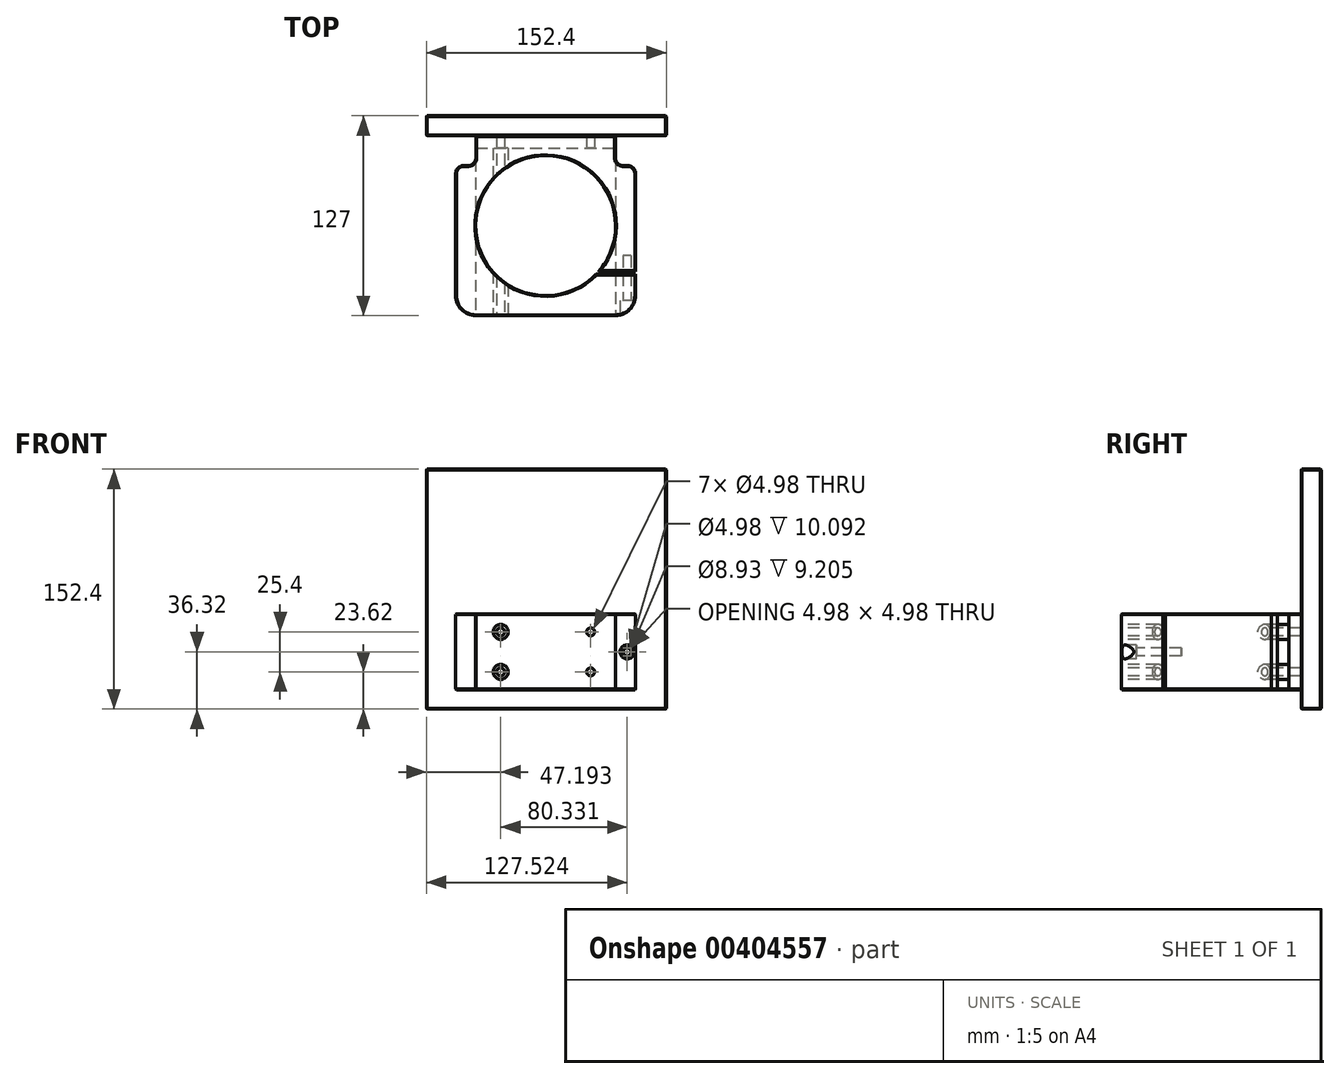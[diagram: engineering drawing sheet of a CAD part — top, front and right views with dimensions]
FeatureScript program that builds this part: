
annotation { "Feature Type Name" : "Feature", "Feature Type Description" : "" }
export const myFeature = defineFeature(function(context is Context, id is Id, definition is map)
    precondition{}
    {
        {
            var Q0;
            Q0=qCreatedBy(makeId("Front.planeOp"),FACE);
            var sketch = newSketch(context, id + "F0", { "sketchPlane" : qUnion([Q0])});
            skLineSegment(sketch, "E0.bottom", {"start": v(57.15, 57.15) * mm, "end": v(-57.15, 57.15) * mm});
            skLineSegment(sketch, "E0.top", {"start": v(57.15, -57.15) * mm, "end": v(-57.15, -57.15) * mm});
            skLineSegment(sketch, "E0.left", {"start": v(57.15, 57.15) * mm, "end": v(57.15, -57.15) * mm});
            skLineSegment(sketch, "E0.right", {"start": v(-57.15, 57.15) * mm, "end": v(-57.15, -57.15) * mm});
            skPoint(sketch, "E0.middle", {"position": v(0, 0) * mm});
            skLineSegment(sketch, "E1", {"start": v(-57.15, 38.1) * mm, "end": v(-44.28, 38.1) * mm});
            skLineSegment(sketch, "E2", {"start": v(-44.28, 57.15) * mm, "end": v(-44.28, 38.1) * mm});
            skLineSegment(sketch, "E3.MirrorCS", {"start": v(44.28, 57.15) * mm, "end": v(44.28, 38.1) * mm});
            skCircle(sketch, "E4", {"center": v(0, 0) * mm, "radius": 44.45 * mm});
            skLineSegment(sketch, "E5.trimOffspring", {"start": v(44.28, 38.1) * mm, "end": v(57.15, 38.1) * mm});
            skSolve(sketch);
        }
        {
            var Q0;
            {var subQ1=sQuery(id+"F0.wireOp",EDGE,"E0.top");Q0=makeQuery(id+"F0.imprint","IMPRINT",FACE,{"disambiguationData":[TD([[makeQuery(id+"F0.imprint","IMPRINT",EDGE,{"derivedFrom":subQ1}),-1.0]])]});}
            extrude(context, id + "F1", {"entities" : qUnion([Q0]), "depth" : 48.26 * mm});
        }
        {
            var Q0;
            Q0=makeQuery(id+"F1.opExtrude","SWEPT_EDGE",EDGE,{"disambiguationData":[OSD([sQuery(id+"F0.wireOp",EDGE,"E3.MirrorCS"),sQuery(id+"F0.wireOp",EDGE,"E5.trimOffspring")])]});
            var Q1;
            Q1=makeQuery(id+"F1.opExtrude","SWEPT_EDGE",EDGE,{"disambiguationData":[OSD([sQuery(id+"F0.wireOp",EDGE,"E0.left"),sQuery(id+"F0.wireOp",EDGE,"E5.trimOffspring")])]});
            var Q2;
            Q2=makeQuery(id+"F1.opExtrude","SWEPT_EDGE",EDGE,{"disambiguationData":[OSD([sQuery(id+"F0.wireOp",EDGE,"E1"),sQuery(id+"F0.wireOp",EDGE,"E2")])]});
            var Q3;
            Q3=makeQuery(id+"F1.opExtrude","SWEPT_EDGE",EDGE,{"disambiguationData":[OSD([sQuery(id+"F0.wireOp",EDGE,"E0.right"),sQuery(id+"F0.wireOp",EDGE,"E1")])]});
            fillet(context, id + "F2", {"entities" : qUnion([Q0, Q1, Q2, Q3]), "radius" : 5.08 * mm, "tangentPropagation" : true, "allowEdgeOverflow" : false});
        }
        {
            var Q0;
            Q0=makeQuery(id+"F1.opExtrude","SWEPT_EDGE",EDGE,{"disambiguationData":[OSD([sQuery(id+"F0.wireOp",EDGE,"E0.top"),sQuery(id+"F0.wireOp",EDGE,"E0.left")])]});
            var Q1;
            Q1=makeQuery(id+"F1.opExtrude","SWEPT_EDGE",EDGE,{"disambiguationData":[OSD([sQuery(id+"F0.wireOp",EDGE,"E0.top"),sQuery(id+"F0.wireOp",EDGE,"E0.right")])]});
            fillet(context, id + "F3", {"entities" : qUnion([Q0, Q1]), "radius" : 12.7 * mm, "tangentPropagation" : true, "allowEdgeOverflow" : false});
        }
        {
            var Q0;
            Q0=makeQuery(id+"F1.opExtrude","CAP_FACE",FACE,{"disambiguationData":[OSD([sQuery(id+"F0.wireOp",EDGE,"E0.bottom"),sQuery(id+"F0.wireOp",EDGE,"E0.top"),sQuery(id+"F0.wireOp",EDGE,"E0.left"),sQuery(id+"F0.wireOp",EDGE,"E0.right"),sQuery(id+"F0.wireOp",EDGE,"E1"),sQuery(id+"F0.wireOp",EDGE,"E2"),sQuery(id+"F0.wireOp",EDGE,"E3.MirrorCS"),sQuery(id+"F0.wireOp",EDGE,"E4"),sQuery(id+"F0.wireOp",EDGE,"E5.trimOffspring")])],"isStart":true});
            var sketch = newSketch(context, id + "F4", { "sketchPlane" : qUnion([Q0])});
            skLineSegment(sketch, "E6.bottom", {"start": v(70.96, -29.14) * mm, "end": v(-5.24, -29.14) * mm});
            skLineSegment(sketch, "E6.top", {"start": v(70.96, -30.73) * mm, "end": v(-5.24, -30.73) * mm});
            skLineSegment(sketch, "E6.left", {"start": v(70.96, -29.14) * mm, "end": v(70.96, -30.73) * mm});
            skLineSegment(sketch, "E6.right", {"start": v(-5.24, -29.14) * mm, "end": v(-5.24, -30.73) * mm});
            skPoint(sketch, "E6.middle", {"position": v(32.86, -29.94) * mm});
            skSolve(sketch);
        }
        {
            var Q0;
            {var subQ0=sQuery(id+"F4.wireOp",EDGE,"E6.bottom");var subQ1=makeQuery(id+"F1.opExtrude","CAP_EDGE",EDGE,{"disambiguationData":[OSD([sQuery(id+"F0.wireOp",EDGE,"E0.right")])],"isStart":true});var subQ2=makeQuery(id+"F4.imprint","INTERSECT",VERTEX,{"derivedFrom":[subQ1,subQ0]});Q0=makeQuery(id+"F4.imprint","IMPRINT",FACE,{"disambiguationData":[TD([[makeQuery(id+"F4.imprint","IMPRINT",EDGE,{"disambiguationData":[TD([[subQ2,-1.0]])],"derivedFrom":subQ0}),1.0]])]});}
            extrude(context, id + "F5", {"entities" : qUnion([Q0]), "operationType" : NewBodyOperationType.REMOVE, "oppositeDirection" : true, "depth" : 50.8 * mm});
        }
        {
            var Q0;
            Q0=makeQuery(id+"F1.opExtrude","CAP_FACE",FACE,{"disambiguationData":[OSD([sQuery(id+"F0.wireOp",EDGE,"E0.bottom"),sQuery(id+"F0.wireOp",EDGE,"E0.top"),sQuery(id+"F0.wireOp",EDGE,"E0.left"),sQuery(id+"F0.wireOp",EDGE,"E0.right"),sQuery(id+"F0.wireOp",EDGE,"E1"),sQuery(id+"F0.wireOp",EDGE,"E2"),sQuery(id+"F0.wireOp",EDGE,"E3.MirrorCS"),sQuery(id+"F0.wireOp",EDGE,"E4"),sQuery(id+"F0.wireOp",EDGE,"E5.trimOffspring")])],"isStart":true});
            var Q1;
            Q1=makeQuery(id+"F1.opExtrude","CAP_FACE",FACE,{"disambiguationData":[OSD([sQuery(id+"F0.wireOp",EDGE,"E0.bottom"),sQuery(id+"F0.wireOp",EDGE,"E0.top"),sQuery(id+"F0.wireOp",EDGE,"E0.left"),sQuery(id+"F0.wireOp",EDGE,"E0.right"),sQuery(id+"F0.wireOp",EDGE,"E1"),sQuery(id+"F0.wireOp",EDGE,"E2"),sQuery(id+"F0.wireOp",EDGE,"E3.MirrorCS"),sQuery(id+"F0.wireOp",EDGE,"E4"),sQuery(id+"F0.wireOp",EDGE,"E5.trimOffspring")])],"isStart":false});
            chamfer(context, id + "F6", {"entities" : qUnion([Q0, Q1]), "width" : 0.5 * mm, "tangentPropagation" : true});
        }
        {
            var Q0;
            Q0=makeQuery(id+"F1.opExtrude","SWEPT_FACE",FACE,{"disambiguationData":[OSD([sQuery(id+"F0.wireOp",EDGE,"E0.top")])]});
            var sketch = newSketch(context, id + "F7", { "sketchPlane" : qUnion([Q0])});
            skLineSegment(sketch, "E7", {"start": v(-44.45, 11.43) * mm, "end": v(44.45, 11.43) * mm, "construction": true});
            skLineSegment(sketch, "E8.MirrorCS", {"start": v(-44.45, 36.83) * mm, "end": v(44.45, 36.83) * mm, "construction": true});
            skLineSegment(sketch, "E9", {"start": v(0, 36.83) * mm, "end": v(0, 11.43) * mm, "construction": true});
            skLineSegment(sketch, "E10", {"start": v(-28.57, 36.83) * mm, "end": v(-28.57, 11.43) * mm, "construction": true});
            skLineSegment(sketch, "E11.MirrorCS", {"start": v(28.58, 36.83) * mm, "end": v(28.58, 11.43) * mm, "construction": true});
            skCircle(sketch, "E12", {"center": v(-28.57, 36.83) * mm, "radius": 2.49 * mm});
            skCircle(sketch, "E13", {"center": v(-28.57, 11.43) * mm, "radius": 2.49 * mm});
            skCircle(sketch, "E14.MirrorC", {"center": v(28.58, 36.83) * mm, "radius": 2.49 * mm});
            skCircle(sketch, "E15.MirrorC", {"center": v(28.58, 11.43) * mm, "radius": 2.49 * mm});
            skSolve(sketch);
        }
        {
            var Q0;
            Q0 = qSketchRegion(id + "F7", true);
            extrude(context, id + "F8", {"entities" : qUnion([Q0]), "operationType" : NewBodyOperationType.REMOVE, "endBound" : BoundingType.THROUGH_ALL, "oppositeDirection" : true, "depth" : 25.4 * mm});
        }
        {
            var Q0;
            Q0=makeQuery(id+"F1.opExtrude","SWEPT_FACE",FACE,{"disambiguationData":[OSD([sQuery(id+"F0.wireOp",EDGE,"E0.top")])]});
            var sketch = newSketch(context, id + "F9", { "sketchPlane" : qUnion([Q0])});
            skCircle(sketch, "E16", {"center": v(-28.57, 36.83) * mm, "radius": 4.76 * mm});
            skCircle(sketch, "E17", {"center": v(-28.57, 11.43) * mm, "radius": 4.76 * mm});
            skCircle(sketch, "E18.MirrorC", {"center": v(28.57, 36.83) * mm, "radius": 4.76 * mm});
            skCircle(sketch, "E19.MirrorC", {"center": v(28.57, 11.43) * mm, "radius": 4.76 * mm});
            skSolve(sketch);
        }
        {
            var Q0;
            Q0=makeQuery(id+"F9.imprint","IMPRINT",FACE,{"disambiguationData":[TD([[makeQuery(id+"F9.imprint","IMPRINT",EDGE,{"derivedFrom":sQuery(id+"F9.wireOp",EDGE,"E17")}),1.0]])]});
            var Q1;
            Q1=makeQuery(id+"F9.imprint","IMPRINT",FACE,{"disambiguationData":[TD([[makeQuery(id+"F9.imprint","IMPRINT",EDGE,{"derivedFrom":sQuery(id+"F9.wireOp",EDGE,"E16")}),1.0]])]});
            var Q2;
            Q2=makeQuery(id+"F9.imprint","IMPRINT",FACE,{"disambiguationData":[TD([[makeQuery(id+"F9.imprint","IMPRINT",EDGE,{"derivedFrom":sQuery(id+"F9.wireOp",EDGE,"E18.MirrorC")}),-1.0]])]});
            var Q3;
            Q3=makeQuery(id+"F9.imprint","IMPRINT",FACE,{"disambiguationData":[TD([[makeQuery(id+"F9.imprint","IMPRINT",EDGE,{"derivedFrom":sQuery(id+"F9.wireOp",EDGE,"E19.MirrorC")}),-1.0]])]});
            extrude(context, id + "F10", {"entities" : qUnion([Q0, Q1, Q2, Q3]), "operationType" : NewBodyOperationType.REMOVE, "oppositeDirection" : true, "depth" : 106.43 * mm});
        }
        {
            var Q0;
            Q0=makeQuery(id+"F1.opExtrude","SWEPT_FACE",FACE,{"disambiguationData":[OSD([sQuery(id+"F0.wireOp",EDGE,"E0.bottom")])]});
            var sketch = newSketch(context, id + "F11", { "sketchPlane" : qUnion([Q0])});
            skLineSegment(sketch, "E20.bottom", {"start": v(75.77, -47.75) * mm, "end": v(-76.63, -47.75) * mm});
            skLineSegment(sketch, "E20.top", {"start": v(75.77, 104.65) * mm, "end": v(-76.63, 104.65) * mm});
            skLineSegment(sketch, "E20.left", {"start": v(75.77, -47.75) * mm, "end": v(75.77, 104.65) * mm});
            skLineSegment(sketch, "E20.right", {"start": v(-76.63, -47.75) * mm, "end": v(-76.63, 104.65) * mm});
            skSolve(sketch);
        }
        {
            var Q0;
            Q0 = qSketchRegion(id + "F11", true);
            extrude(context, id + "F12", {"entities" : qUnion([Q0]), "depth" : 12.7 * mm});
        }
        {
            var Q0;
            Q0=makeQuery(id+"F12.opExtrude","CAP_FACE",FACE,{"disambiguationData":[OSD([sQuery(id+"F11.wireOp",EDGE,"E20.bottom"),sQuery(id+"F11.wireOp",EDGE,"E20.top"),sQuery(id+"F11.wireOp",EDGE,"E20.left"),sQuery(id+"F11.wireOp",EDGE,"E20.right")])],"isStart":true});
            var Q1;
            Q1=makeQuery(id+"F12.opExtrude","CAP_FACE",FACE,{"disambiguationData":[OSD([sQuery(id+"F11.wireOp",EDGE,"E20.bottom"),sQuery(id+"F11.wireOp",EDGE,"E20.top"),sQuery(id+"F11.wireOp",EDGE,"E20.left"),sQuery(id+"F11.wireOp",EDGE,"E20.right")])],"isStart":false});
            var Q2;
            Q2=makeQuery(id+"F12.opExtrude","SWEPT_FACE",FACE,{"disambiguationData":[OSD([sQuery(id+"F11.wireOp",EDGE,"E20.top")])]});
            var Q3;
            Q3=makeQuery(id+"F12.opExtrude","SWEPT_FACE",FACE,{"disambiguationData":[OSD([sQuery(id+"F11.wireOp",EDGE,"E20.bottom")])]});
            chamfer(context, id + "F13", {"entities" : qUnion([Q0, Q1, Q2, Q3]), "width" : 0.5 * mm, "tangentPropagation" : true});
        }
        {
            var Q0;
            Q0=makeQuery(id+"F1.opExtrude","SWEPT_BODY",BODY,{"disambiguationData":[OSD([sQuery(id+"F0.wireOp",EDGE,"E0.bottom"),sQuery(id+"F0.wireOp",EDGE,"E0.top"),sQuery(id+"F0.wireOp",EDGE,"E0.left"),sQuery(id+"F0.wireOp",EDGE,"E0.right"),sQuery(id+"F0.wireOp",EDGE,"E1"),sQuery(id+"F0.wireOp",EDGE,"E2"),sQuery(id+"F0.wireOp",EDGE,"E3.MirrorCS"),sQuery(id+"F0.wireOp",EDGE,"E4"),sQuery(id+"F0.wireOp",EDGE,"E5.trimOffspring")])]});
            var Q1;
            Q1=qCreatedBy(makeId("Front.planeOp"),FACE);
            transform(context, id + "F14", {"entities" : qUnion([Q0]), "transformType" : TransformType.TRANSLATION_DISTANCE, "transformDirection" : qUnion([Q1]), "distance" : 12.7 * mm, "oppositeDirection" : true, "makeCopy" : false});
        }
        {
            var Q0;
            Q0=makeQuery(id+"F1.opExtrude","SWEPT_FACE",FACE,{"disambiguationData":[OSD([sQuery(id+"F0.wireOp",EDGE,"E0.top")])]});
            var sketch = newSketch(context, id + "F15", { "sketchPlane" : qUnion([Q0])});
            skLineSegment(sketch, "E21", {"start": v(-57.15, 11.43) * mm, "end": v(57.15, 11.43) * mm, "construction": true});
            skCircle(sketch, "E22", {"center": v(-51.76, 11.43) * mm, "radius": 2.49 * mm});
            skCircle(sketch, "E23", {"center": v(-51.76, 11.43) * mm, "radius": 4.47 * mm});
            skSolve(sketch);
        }
        {
            var Q0;
            Q0=makeQuery(id+"F15.imprint","IMPRINT",FACE,{"disambiguationData":[TD([[makeQuery(id+"F15.imprint","IMPRINT",EDGE,{"derivedFrom":sQuery(id+"F15.wireOp",EDGE,"E22")}),1.0]])]});
            extrude(context, id + "F16", {"entities" : qUnion([Q0]), "operationType" : NewBodyOperationType.REMOVE, "oppositeDirection" : true, "depth" : 38.1 * mm});
        }
        {
            var Q0;
            Q0=makeQuery(id+"F15.imprint","IMPRINT",FACE,{"disambiguationData":[TD([[makeQuery(id+"F15.imprint","IMPRINT",EDGE,{"derivedFrom":sQuery(id+"F15.wireOp",EDGE,"E22")}),-1.0]])]});
            extrude(context, id + "F17", {"entities" : qUnion([Q0]), "operationType" : NewBodyOperationType.REMOVE, "oppositeDirection" : true, "depth" : 9.52 * mm});
        }
        {
            var Q0;
            Q0=makeQuery(id+"F1.opExtrude","SWEPT_BODY",BODY,{"disambiguationData":[OSD([sQuery(id+"F0.wireOp",EDGE,"E0.bottom"),sQuery(id+"F0.wireOp",EDGE,"E0.top"),sQuery(id+"F0.wireOp",EDGE,"E0.left"),sQuery(id+"F0.wireOp",EDGE,"E0.right"),sQuery(id+"F0.wireOp",EDGE,"E1"),sQuery(id+"F0.wireOp",EDGE,"E2"),sQuery(id+"F0.wireOp",EDGE,"E3.MirrorCS"),sQuery(id+"F0.wireOp",EDGE,"E4"),sQuery(id+"F0.wireOp",EDGE,"E5.trimOffspring")])]});
            var Q1;
            Q1=makeQuery(id+"F12.opExtrude","SWEPT_BODY",BODY,{"disambiguationData":[OSD([sQuery(id+"F11.wireOp",EDGE,"E20.bottom"),sQuery(id+"F11.wireOp",EDGE,"E20.top"),sQuery(id+"F11.wireOp",EDGE,"E20.left"),sQuery(id+"F11.wireOp",EDGE,"E20.right")])]});
            var Q2;
            Q2=sQuery(id+"F15.wireOp",EDGE,"E22");
            transform(context, id + "F18", {"entities" : qUnion([Q0, Q1]), "transformType" : TransformType.ROTATION, "transformAxis" : qUnion([Q2]), "angle" : 180 * degree, "makeCopy" : false});
        }
        {
            var Q0;
            Q0=makeQuery(id+"F1.opExtrude","SWEPT_BODY",BODY,{"disambiguationData":[OSD([sQuery(id+"F0.wireOp",EDGE,"E0.bottom"),sQuery(id+"F0.wireOp",EDGE,"E0.top"),sQuery(id+"F0.wireOp",EDGE,"E0.left"),sQuery(id+"F0.wireOp",EDGE,"E0.right"),sQuery(id+"F0.wireOp",EDGE,"E1"),sQuery(id+"F0.wireOp",EDGE,"E2"),sQuery(id+"F0.wireOp",EDGE,"E3.MirrorCS"),sQuery(id+"F0.wireOp",EDGE,"E4"),sQuery(id+"F0.wireOp",EDGE,"E5.trimOffspring")])]});
            var Q1;
            Q1=makeQuery(id+"F12.opExtrude","SWEPT_BODY",BODY,{"disambiguationData":[OSD([sQuery(id+"F11.wireOp",EDGE,"E20.bottom"),sQuery(id+"F11.wireOp",EDGE,"E20.top"),sQuery(id+"F11.wireOp",EDGE,"E20.left"),sQuery(id+"F11.wireOp",EDGE,"E20.right")])]});
            var Q2;
            {var subQ0=sQuery(id+"F11.wireOp",EDGE,"E20.bottom");Q2=makeQuery(id+"F13.opChamfer","BLEND_EDGE",EDGE,{"blendedFrom":[makeQuery(id+"F12.opExtrude","CAP_EDGE",EDGE,{"disambiguationData":[OSD([subQ0])],"isStart":true}),makeQuery(id+"F12.opExtrude","SWEPT_FACE",FACE,{"disambiguationData":[OSD([subQ0])]})],"blendedInto":[makeQuery(id+"F12.opExtrude","SWEPT_FACE",FACE,{"disambiguationData":[OSD([subQ0])]})]});}
            transform(context, id + "F20", {"entities" : qUnion([Q0, Q1]), "transformType" : TransformType.ROTATION, "transformAxis" : qUnion([Q2]), "angle" : 90 * degree, "makeCopy" : false});
        }
    });
